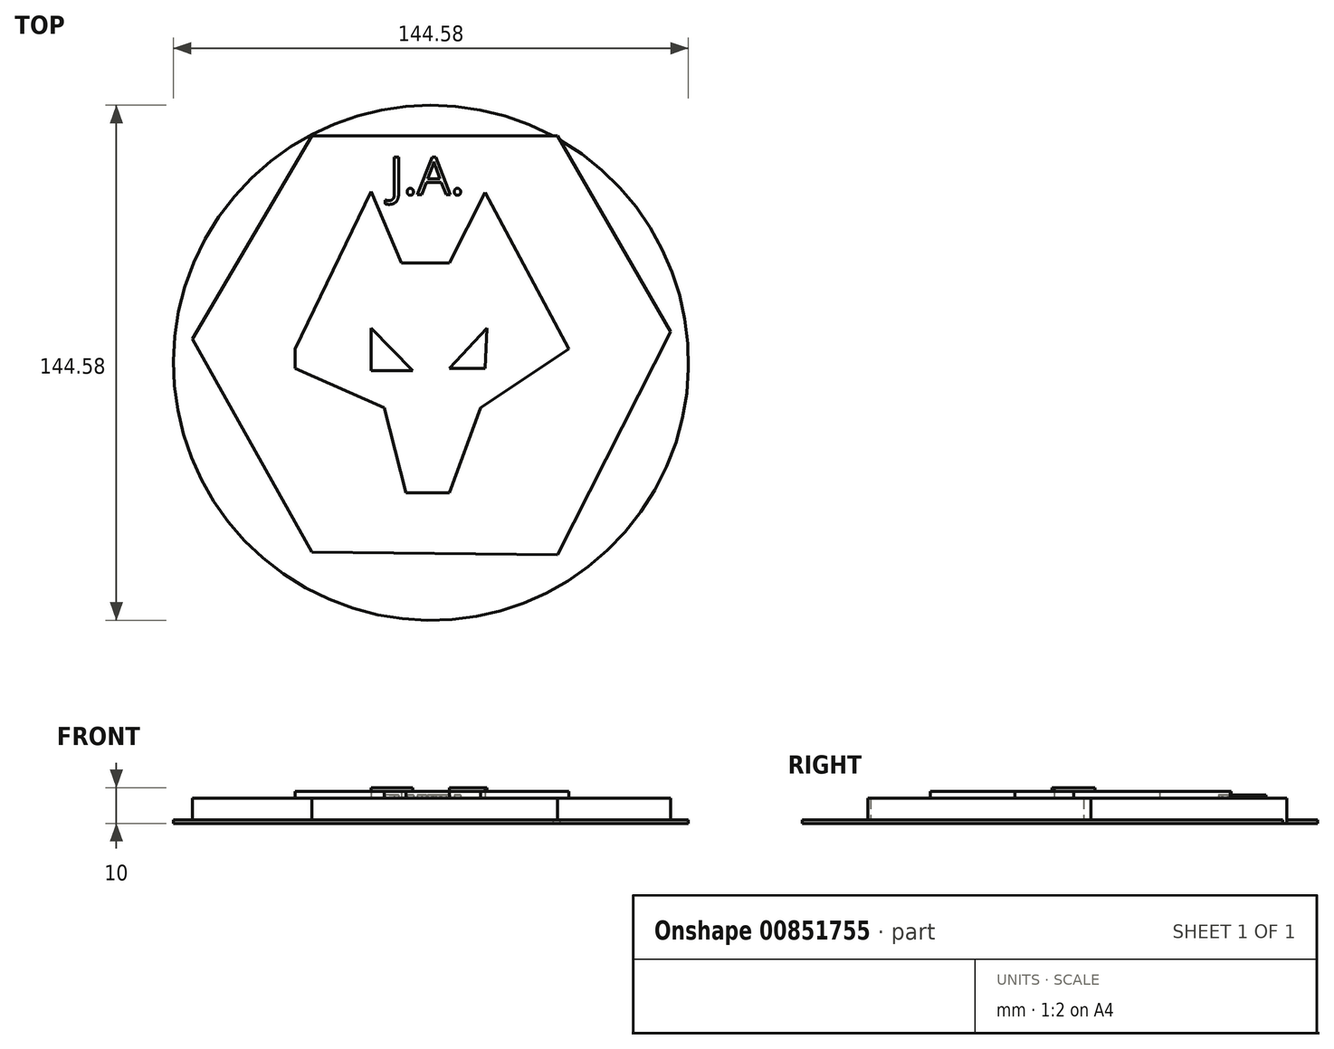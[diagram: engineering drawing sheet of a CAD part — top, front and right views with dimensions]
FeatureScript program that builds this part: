
annotation { "Feature Type Name" : "Feature", "Feature Type Description" : "" }
export const myFeature = defineFeature(function(context is Context, id is Id, definition is map)
    precondition{}
    {
        {
            var Q0;
            Q0=qCreatedBy(makeId("Top.planeOp"),FACE);
            var sketch = newSketch(context, id + "F0", { "sketchPlane" : qUnion([Q0])});
            skLineSegment(sketch, "E0", {"start": v(-33.41, 59.86) * mm, "end": v(-67, 2.77) * mm});
            skLineSegment(sketch, "E1", {"start": v(-67, 2.77) * mm, "end": v(-33.43, -56.95) * mm});
            skLineSegment(sketch, "E2", {"start": v(-33.43, -56.95) * mm, "end": v(35.54, -57.74) * mm});
            skLineSegment(sketch, "E3", {"start": v(35.54, -57.74) * mm, "end": v(67.26, 4.82) * mm});
            skLineSegment(sketch, "E4", {"start": v(67.26, 4.82) * mm, "end": v(35.54, 59.86) * mm});
            skLineSegment(sketch, "E5", {"start": v(35.54, 59.86) * mm, "end": v(-33.41, 59.86) * mm});
            skLineSegment(sketch, "E6", {"start": v(-25.77, 47.17) * mm, "end": v(-53.51, 0) * mm});
            skLineSegment(sketch, "E7", {"start": v(-53.51, 0) * mm, "end": v(-27.88, -45.59) * mm});
            skLineSegment(sketch, "E8", {"start": v(-27.88, -45.59) * mm, "end": v(27.09, -45.59) * mm});
            skLineSegment(sketch, "E9", {"start": v(27.09, -45.59) * mm, "end": v(53.9, 0) * mm});
            skLineSegment(sketch, "E10", {"start": v(53.9, 0) * mm, "end": v(27.09, 47.14) * mm});
            skLineSegment(sketch, "E11", {"start": v(27.09, 47.14) * mm, "end": v(-25.77, 47.17) * mm});
            skLineSegment(sketch, "E12", {"start": v(-16.78, 44.26) * mm, "end": v(-38.19, 0) * mm});
            skLineSegment(sketch, "E13", {"start": v(-38.19, 0) * mm, "end": v(-38.19, -5.42) * mm});
            skLineSegment(sketch, "E14", {"start": v(-38.19, -5.42) * mm, "end": v(-13.08, -16.52) * mm});
            skLineSegment(sketch, "E15", {"start": v(-13.08, -16.52) * mm, "end": v(-7, -40.3) * mm});
            skLineSegment(sketch, "E16", {"start": v(-7, -40.3) * mm, "end": v(5.15, -40.3) * mm});
            skLineSegment(sketch, "E17", {"start": v(5.15, -40.3) * mm, "end": v(13.87, -16.52) * mm});
            skLineSegment(sketch, "E18", {"start": v(13.87, -16.52) * mm, "end": v(38.71, 0) * mm});
            skLineSegment(sketch, "E19", {"start": v(5.15, 24.18) * mm, "end": v(-8.32, 24.18) * mm});
            skLineSegment(sketch, "E20", {"start": v(-8.32, 24.18) * mm, "end": v(-16.78, 44.26) * mm});
            skLineSegment(sketch, "E21", {"start": v(5.15, 24.18) * mm, "end": v(15.2, 44) * mm});
            skLineSegment(sketch, "E22", {"start": v(15.2, 44) * mm, "end": v(38.71, 0) * mm});
            skLineSegment(sketch, "E23", {"start": v(15.72, 5.95) * mm, "end": v(5.15, -5.42) * mm});
            skLineSegment(sketch, "E24", {"start": v(5.15, -5.42) * mm, "end": v(15.16, -5.42) * mm});
            skLineSegment(sketch, "E25", {"start": v(15.16, -5.42) * mm, "end": v(15.72, 5.95) * mm});
            skLineSegment(sketch, "E26", {"start": v(-16.78, 5.95) * mm, "end": v(-16.78, -6.06) * mm});
            skLineSegment(sketch, "E27", {"start": v(-16.78, -6.06) * mm, "end": v(-5.16, -6.07) * mm});
            skLineSegment(sketch, "E28", {"start": v(-5.16, -6.07) * mm, "end": v(-16.78, 5.95) * mm});
            skSolve(sketch);
        }
        {
            var Q0;
            Q0 = qSketchRegion(id + "F0", true);
            var Q1;
            Q1=makeQuery(id+"F0.imprint","IMPRINT",FACE,{"disambiguationData":[TD([[makeQuery(id+"F0.imprint","IMPRINT",EDGE,{"derivedFrom":sQuery(id+"F0.wireOp",EDGE,"E6")}),1.0]])]});
            extrude(context, id + "F1", {"entities" : qUnion([Q0, Q1]), "depth" : 7 * mm, "offsetDistance" : 25 * mm});
        }
        {
            var Q0;
            Q0=qCreatedBy(makeId("Top.planeOp"),FACE);
            var sketch = newSketch(context, id + "F2", { "sketchPlane" : qUnion([Q0])});
            skCircle(sketch, "E29", {"center": v(0, -3.83) * mm, "radius": 72.29 * mm});
            skSolve(sketch);
        }
        {
            var Q0;
            Q0=makeQuery(id+"F2.imprint","IMPRINT",FACE,{"disambiguationData":[TD([[makeQuery(id+"F2.imprint","IMPRINT",EDGE,{"derivedFrom":sQuery(id+"F2.wireOp",EDGE,"E29")}),1.0]])]});
            extrude(context, id + "F3", {"entities" : qUnion([Q0]), "operationType" : NewBodyOperationType.ADD, "depth" : 1 * mm, "offsetDistance" : 25 * mm});
        }
        {
            var Q0;
            Q0=makeQuery(id+"F0.imprint","IMPRINT",FACE,{"disambiguationData":[TD([[makeQuery(id+"F0.imprint","IMPRINT",EDGE,{"derivedFrom":sQuery(id+"F0.wireOp",EDGE,"E23")}),1.0]])]});
            var Q1;
            Q1=makeQuery(id+"F0.imprint","IMPRINT",FACE,{"disambiguationData":[TD([[makeQuery(id+"F0.imprint","IMPRINT",EDGE,{"derivedFrom":sQuery(id+"F0.wireOp",EDGE,"E26")}),1.0]])]});
            extrude(context, id + "F4", {"entities" : qUnion([Q0, Q1]), "operationType" : NewBodyOperationType.ADD, "depth" : 2 * mm, "offsetDistance" : 25 * mm});
        }
        {
            var Q0;
            Q0=makeQuery(id+"F1.opExtrude","CAP_FACE",FACE,{"disambiguationData":[OSD([sQuery(id+"F0.wireOp",EDGE,"E0"),sQuery(id+"F0.wireOp",EDGE,"E1"),sQuery(id+"F0.wireOp",EDGE,"E2"),sQuery(id+"F0.wireOp",EDGE,"E3"),sQuery(id+"F0.wireOp",EDGE,"E4"),sQuery(id+"F0.wireOp",EDGE,"E5"),sQuery(id+"F0.wireOp",EDGE,"E12"),sQuery(id+"F0.wireOp",EDGE,"E13"),sQuery(id+"F0.wireOp",EDGE,"E14"),sQuery(id+"F0.wireOp",EDGE,"E15"),sQuery(id+"F0.wireOp",EDGE,"E16"),sQuery(id+"F0.wireOp",EDGE,"E17"),sQuery(id+"F0.wireOp",EDGE,"E18"),sQuery(id+"F0.wireOp",EDGE,"E19"),sQuery(id+"F0.wireOp",EDGE,"E20"),sQuery(id+"F0.wireOp",EDGE,"E21"),sQuery(id+"F0.wireOp",EDGE,"E22")])],"isStart":false});
            var sketch = newSketch(context, id + "F5", { "sketchPlane" : qUnion([Q0])});
            skText(sketch, "E30", { "text": "J.A.", "fontName": "OpenSans-Regular.ttf"});
            const initialGuessF5  = {"E30": [-0.01167, 0.04338, 1, 0, 0.0106]};
            skSetInitialGuess(sketch, initialGuessF5);
            skSolve(sketch);
        }
        {
            var Q0;
            Q0 = qSketchRegion(id + "F5", true);
            extrude(context, id + "F6", {"entities" : qUnion([Q0]), "operationType" : NewBodyOperationType.ADD, "depth" : 1 * mm, "offsetDistance" : 25 * mm});
        }
        {
            var Q0;
            Q0=makeQuery(id+"F3.boolean.opBoolean","SPLIT",FACE,{"disambiguationData":[TD([makeQuery(id+"F1.opExtrude","SWEPT_FACE",FACE,{"disambiguationData":[OSD([sQuery(id+"F0.wireOp",EDGE,"E12")])]})])],"derivedFrom":makeQuery(id+"F3.opExtrude","CAP_FACE",FACE,{"disambiguationData":[OSD([sQuery(id+"F2.wireOp",EDGE,"E29")])],"isStart":false})});
            var Q1;
            Q1=makeQuery(id+"F4.opExtrude","CAP_FACE",FACE,{"disambiguationData":[OSD([sQuery(id+"F0.wireOp",EDGE,"E26"),sQuery(id+"F0.wireOp",EDGE,"E27"),sQuery(id+"F0.wireOp",EDGE,"E28")])],"isStart":false});
            var Q2;
            Q2=makeQuery(id+"F4.opExtrude","CAP_FACE",FACE,{"disambiguationData":[OSD([sQuery(id+"F0.wireOp",EDGE,"E23"),sQuery(id+"F0.wireOp",EDGE,"E24"),sQuery(id+"F0.wireOp",EDGE,"E25")])],"isStart":false});
            extrude(context, id + "F7", {"entities" : qUnion([Q0, Q1, Q2]), "operationType" : NewBodyOperationType.ADD, "depth" : 8 * mm, "offsetDistance" : 25 * mm});
        }
    });
